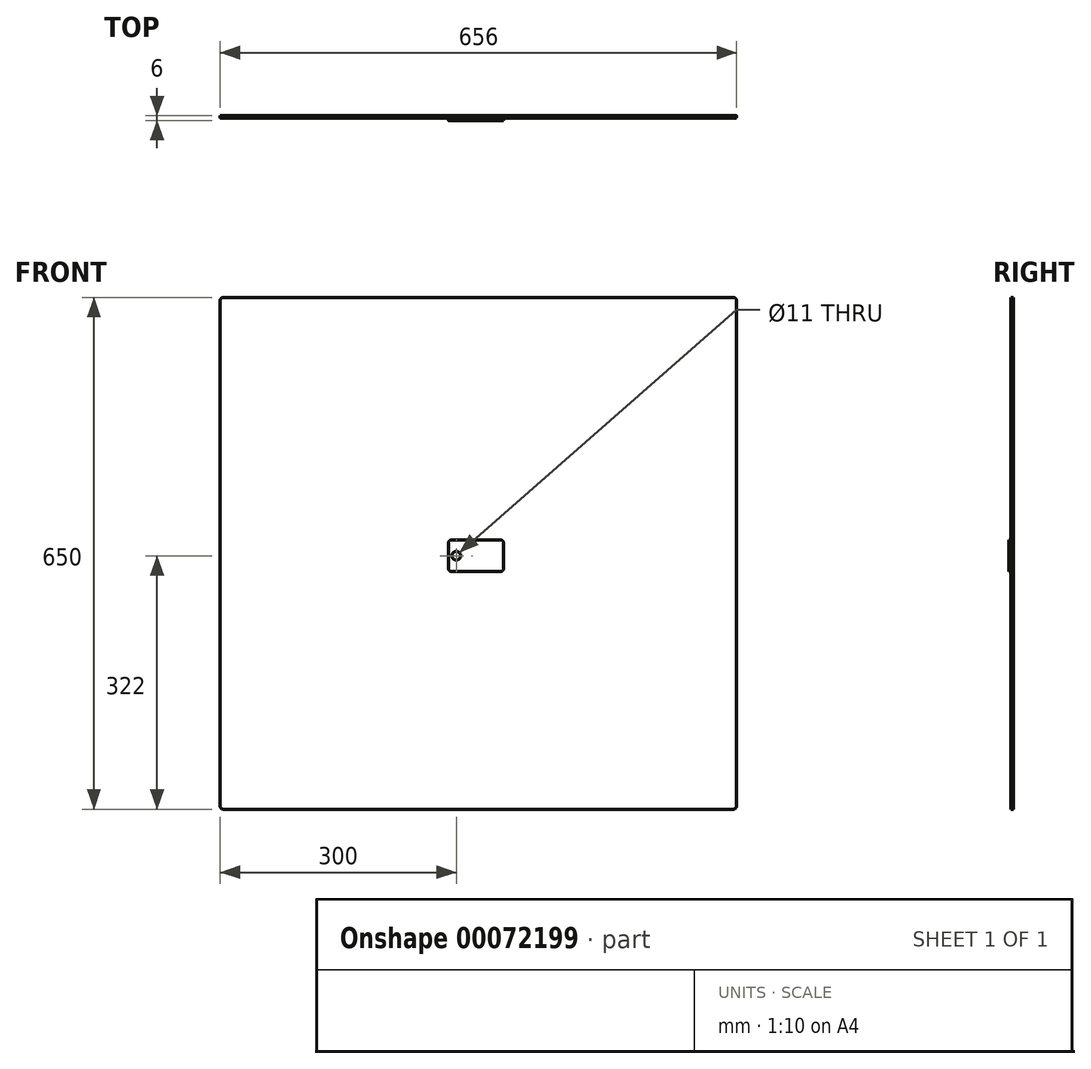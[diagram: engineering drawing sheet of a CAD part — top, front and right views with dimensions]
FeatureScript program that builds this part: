
annotation { "Feature Type Name" : "Feature", "Feature Type Description" : "" }
export const myFeature = defineFeature(function(context is Context, id is Id, definition is map)
    precondition{}
    {
        {
            var Q0;
            Q0=qCreatedBy(makeId("Front.planeOp"),FACE);
            var sketch = newSketch(context, id + "F0", { "sketchPlane" : qUnion([Q0])});
            skLineSegment(sketch, "E0.bottom", {"start": v(-35, 20) * mm, "end": v(35, 20) * mm});
            skLineSegment(sketch, "E0.top", {"start": v(-35, -20) * mm, "end": v(35, -20) * mm});
            skLineSegment(sketch, "E0.left", {"start": v(-35, 20) * mm, "end": v(-35, -20) * mm});
            skLineSegment(sketch, "E0.right", {"start": v(35, 20) * mm, "end": v(35, -20) * mm});
            skSolve(sketch);
        }
        {
            var Q0;
            Q0=makeQuery(id+"F0.imprint","IMPRINT",FACE,{"disambiguationData":[TD([[makeQuery(id+"F0.imprint","IMPRINT",EDGE,{"derivedFrom":sQuery(id+"F0.wireOp",EDGE,"E0.bottom")}),-1.0]])]});
            extrude(context, id + "F1", {"entities" : qUnion([Q0]), "depth" : 6 * mm});
        }
        {
            var Q0;
            Q0=makeQuery(id+"F1.opExtrude","SWEPT_EDGE",EDGE,{"disambiguationData":[OSD([sQuery(id+"F0.wireOp",EDGE,"E0.bottom"),sQuery(id+"F0.wireOp",EDGE,"E0.right")])]});
            var Q1;
            Q1=makeQuery(id+"F1.opExtrude","SWEPT_EDGE",EDGE,{"disambiguationData":[OSD([sQuery(id+"F0.wireOp",EDGE,"E0.top"),sQuery(id+"F0.wireOp",EDGE,"E0.right")])]});
            var Q2;
            Q2=makeQuery(id+"F1.opExtrude","SWEPT_EDGE",EDGE,{"disambiguationData":[OSD([sQuery(id+"F0.wireOp",EDGE,"E0.bottom"),sQuery(id+"F0.wireOp",EDGE,"E0.left")])]});
            var Q3;
            Q3=makeQuery(id+"F1.opExtrude","SWEPT_EDGE",EDGE,{"disambiguationData":[OSD([sQuery(id+"F0.wireOp",EDGE,"E0.top"),sQuery(id+"F0.wireOp",EDGE,"E0.left")])]});
            fillet(context, id + "F2", {"entities" : qUnion([Q0, Q1, Q2, Q3]), "radius" : 4 * mm, "tangentPropagation" : true, "allowEdgeOverflow" : false});
        }
        {
            var Q0;
            Q0=makeQuery(id+"F1.opExtrude","CAP_FACE",FACE,{"disambiguationData":[OSD([sQuery(id+"F0.wireOp",EDGE,"E0.bottom"),sQuery(id+"F0.wireOp",EDGE,"E0.top"),sQuery(id+"F0.wireOp",EDGE,"E0.left"),sQuery(id+"F0.wireOp",EDGE,"E0.right")])],"isStart":false});
            var sketch = newSketch(context, id + "F3", { "sketchPlane" : qUnion([Q0])});
            skPoint(sketch, "E1", {"position": v(-25, 0) * mm});
            skSolve(sketch);
        }
        {
            var Q0;
            Q0=sQuery(id+"F3.wireOp",VERTEX,"E1");
            var Q1;
            Q1=makeQuery(id+"F1.opExtrude","SWEPT_BODY",BODY,{"disambiguationData":[OSD([sQuery(id+"F0.wireOp",EDGE,"E0.bottom"),sQuery(id+"F0.wireOp",EDGE,"E0.top"),sQuery(id+"F0.wireOp",EDGE,"E0.left"),sQuery(id+"F0.wireOp",EDGE,"E0.right")])]});
            hole(context, id + "F4", {"style" : HoleStyle.SIMPLE, "endStyle" : HoleEndStyle.THROUGH, "holeDiameter" : 11 * mm, "locations" : qUnion([Q0]), "scope" : qUnion([Q1]), "isTappedThrough" : true});
        }
        {
            var Q0;
            Q0=qCreatedBy(makeId("Front.planeOp"),FACE);
            var sketch = newSketch(context, id + "F5", { "sketchPlane" : qUnion([Q0])});
            skLineSegment(sketch, "E2.bottom", {"start": v(-325, 328) * mm, "end": v(331, 328) * mm});
            skLineSegment(sketch, "E2.top", {"start": v(-325, -322) * mm, "end": v(331, -322) * mm});
            skLineSegment(sketch, "E2.left", {"start": v(-325, 328) * mm, "end": v(-325, -322) * mm});
            skLineSegment(sketch, "E2.right", {"start": v(331, 328) * mm, "end": v(331, -322) * mm});
            skSolve(sketch);
        }
        {
            var Q0;
            Q0=makeQuery(id+"F5.imprint","IMPRINT",FACE,{"disambiguationData":[TD([[makeQuery(id+"F5.imprint","IMPRINT",EDGE,{"derivedFrom":sQuery(id+"F5.wireOp",EDGE,"E2.bottom")}),-1.0]])]});
            extrude(context, id + "F6", {"entities" : qUnion([Q0]), "depth" : 3 * mm});
        }
        {
            var Q0;
            Q0=makeQuery(id+"F6.opExtrude","SWEPT_EDGE",EDGE,{"disambiguationData":[OSD([sQuery(id+"F5.wireOp",EDGE,"E2.bottom"),sQuery(id+"F5.wireOp",EDGE,"E2.right")])]});
            var Q1;
            Q1=makeQuery(id+"F6.opExtrude","SWEPT_EDGE",EDGE,{"disambiguationData":[OSD([sQuery(id+"F5.wireOp",EDGE,"E2.bottom"),sQuery(id+"F5.wireOp",EDGE,"E2.left")])]});
            var Q2;
            Q2=makeQuery(id+"F6.opExtrude","SWEPT_EDGE",EDGE,{"disambiguationData":[OSD([sQuery(id+"F5.wireOp",EDGE,"E2.top"),sQuery(id+"F5.wireOp",EDGE,"E2.right")])]});
            var Q3;
            Q3=makeQuery(id+"F6.opExtrude","SWEPT_EDGE",EDGE,{"disambiguationData":[OSD([sQuery(id+"F5.wireOp",EDGE,"E2.top"),sQuery(id+"F5.wireOp",EDGE,"E2.left")])]});
            fillet(context, id + "F7", {"entities" : qUnion([Q0, Q1, Q2, Q3]), "radius" : 4 * mm, "tangentPropagation" : true, "allowEdgeOverflow" : false});
        }
    });
